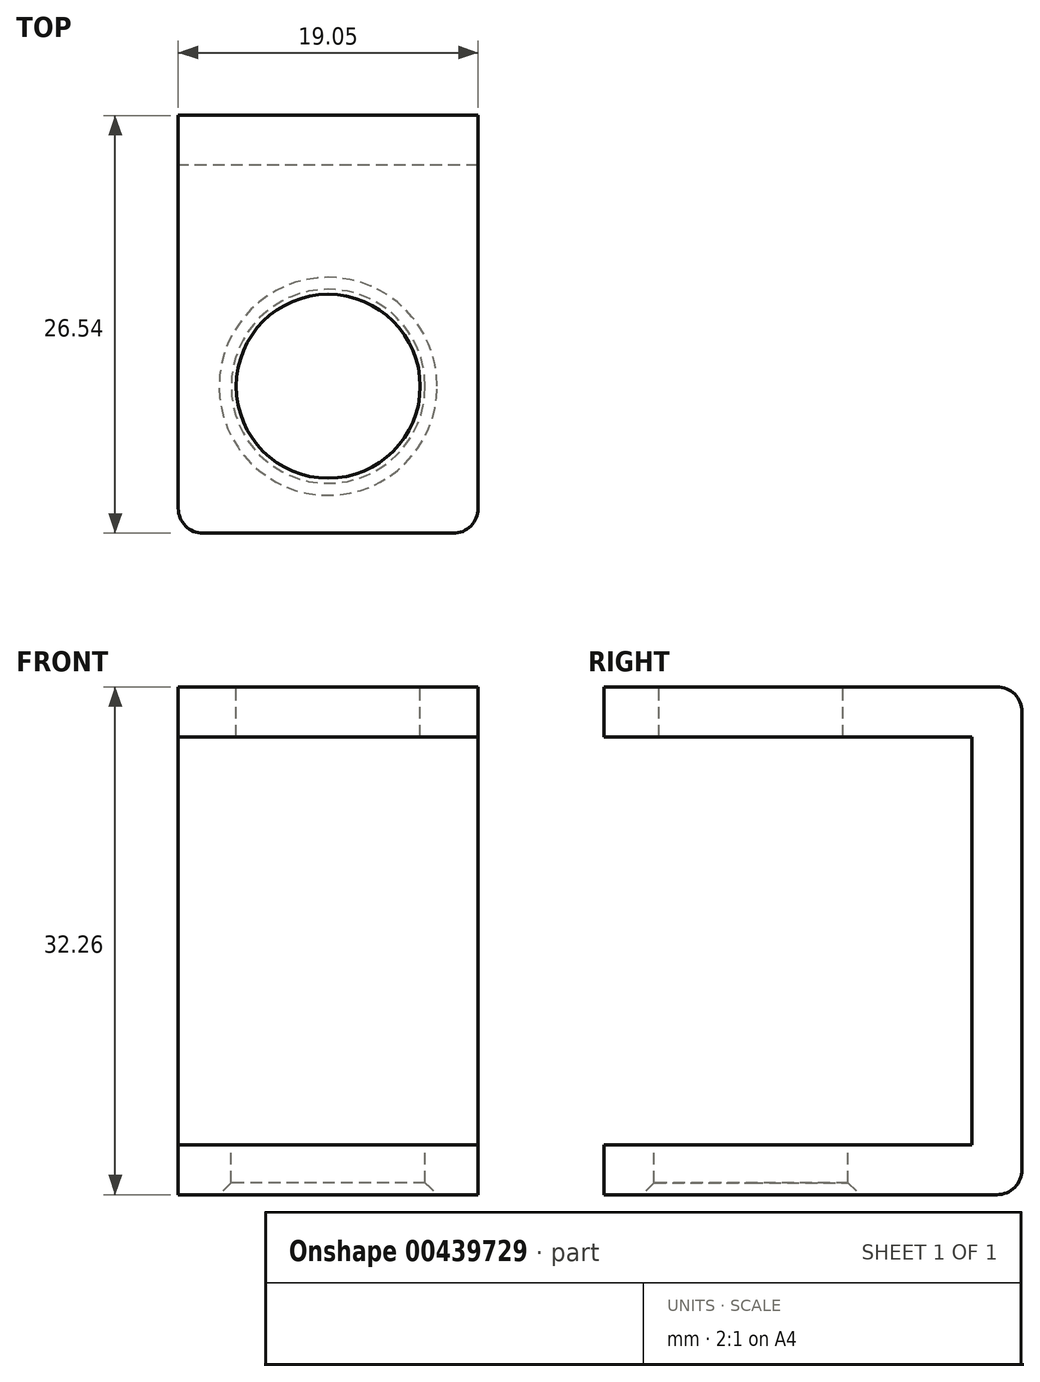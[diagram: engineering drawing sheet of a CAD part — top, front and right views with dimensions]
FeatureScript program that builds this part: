
annotation { "Feature Type Name" : "Feature", "Feature Type Description" : "" }
export const myFeature = defineFeature(function(context is Context, id is Id, definition is map)
    precondition{}
    {
        {
            var Q0;
            Q0=qCreatedBy(makeId("Right.planeOp"),FACE);
            var sketch = newSketch(context, id + "F0", { "sketchPlane" : qUnion([Q0])});
            skLineSegment(sketch, "E0.bottom", {"start": v(0, 0) * mm, "end": v(26.54, 0) * mm});
            skLineSegment(sketch, "E0.top", {"start": v(0, 3.18) * mm, "end": v(23.37, 3.18) * mm});
            skLineSegment(sketch, "E0.left", {"start": v(0, 0) * mm, "end": v(0, 3.18) * mm});
            skLineSegment(sketch, "E1.bottom", {"start": v(0, 32.26) * mm, "end": v(26.54, 32.26) * mm});
            skLineSegment(sketch, "E1.top", {"start": v(0, 29.08) * mm, "end": v(23.37, 29.08) * mm});
            skLineSegment(sketch, "E2", {"start": v(0, 32.26) * mm, "end": v(0, 29.08) * mm});
            skLineSegment(sketch, "E3", {"start": v(23.37, 3.18) * mm, "end": v(23.37, 29.08) * mm});
            skLineSegment(sketch, "E4", {"start": v(26.54, 0) * mm, "end": v(26.54, 32.26) * mm});
            skLineSegment(sketch, "E5", {"start": v(23.37, 29.08) * mm, "end": v(26.54, 29.08) * mm, "construction": true});
            skLineSegment(sketch, "E6", {"start": v(3.18, 21.78) * mm, "end": v(15.37, 21.78) * mm, "construction": true});
            skSolve(sketch);
        }
        {
            var Q0;
            Q0=qSketchRegion(id+"F0",true);
            extrude(context, id + "F1", {"entities" : qUnion([Q0]), "depth" : 19.05 * mm});
        }
        {
            var Q0;
            Q0=makeQuery(id+"F1.opExtrude","SWEPT_FACE",FACE,{"disambiguationData":[OSD([sQuery(id+"F0.wireOp",EDGE,"E0.top")])]});
            var sketch = newSketch(context, id + "F2", { "sketchPlane" : qUnion([Q0])});
            skCircle(sketch, "E7", {"center": v(9.53, 9.33) * mm, "radius": 6.16 * mm});
            skLineSegment(sketch, "E8", {"start": v(9.53, 0) * mm, "end": v(9.53, 9.33) * mm, "construction": true});
            skPoint(sketch, "E9.orphan", {"position": v(19.05, 11.68) * mm});
            skPoint(sketch, "E10", {"position": v(9.53, 3.18) * mm});
            skSolve(sketch);
        }
        {
            var Q0;
            Q0=qSketchRegion(id+"F2",true);
            extrude(context, id + "F3", {"entities" : qUnion([Q0]), "operationType" : NewBodyOperationType.REMOVE, "oppositeDirection" : true, "depth" : 25.4 * mm});
        }
        {
            var Q0;
            Q0=makeQuery(id+"F1.opExtrude","SWEPT_FACE",FACE,{"disambiguationData":[OSD([sQuery(id+"F0.wireOp",EDGE,"E1.bottom")])]});
            var sketch = newSketch(context, id + "F4", { "sketchPlane" : qUnion([Q0])});
            skCircle(sketch, "E11", {"center": v(9.53, 9.33) * mm, "radius": 5.84 * mm});
            skLineSegment(sketch, "E12", {"start": v(9.53, 9.33) * mm, "end": v(9.53, 0) * mm, "construction": true});
            skSolve(sketch);
        }
        {
            var Q0;
            Q0 = qSketchRegion(id + "F4", true);
            extrude(context, id + "F5", {"entities" : qUnion([Q0]), "operationType" : NewBodyOperationType.REMOVE, "endBound" : BoundingType.UP_TO_NEXT, "oppositeDirection" : true, "depth" : 25.4 * mm});
        }
        {
            var Q0;
            Q0=makeQuery(id+"F1.opExtrude","CAP_EDGE",EDGE,{"disambiguationData":[OSD([sQuery(id+"F0.wireOp",EDGE,"E2")])],"isStart":false});
            var Q1;
            Q1=makeQuery(id+"F1.opExtrude","CAP_EDGE",EDGE,{"disambiguationData":[OSD([sQuery(id+"F0.wireOp",EDGE,"E2")])],"isStart":true});
            var Q2;
            Q2=makeQuery(id+"F1.opExtrude","CAP_EDGE",EDGE,{"disambiguationData":[OSD([sQuery(id+"F0.wireOp",EDGE,"E0.left")])],"isStart":true});
            var Q3;
            Q3=makeQuery(id+"F1.opExtrude","CAP_EDGE",EDGE,{"disambiguationData":[OSD([sQuery(id+"F0.wireOp",EDGE,"E0.left")])],"isStart":false});
            var Q4;
            Q4=makeQuery(id+"F1.opExtrude","SWEPT_EDGE",EDGE,{"disambiguationData":[OSD([sQuery(id+"F0.wireOp",EDGE,"E1.bottom"),sQuery(id+"F0.wireOp",EDGE,"E4")])]});
            var Q5;
            Q5=makeQuery(id+"F1.opExtrude","SWEPT_EDGE",EDGE,{"disambiguationData":[OSD([sQuery(id+"F0.wireOp",EDGE,"E0.bottom"),sQuery(id+"F0.wireOp",EDGE,"E4")])]});
            fillet(context, id + "F6", {"entities" : qUnion([Q0, Q1, Q2, Q3, Q4, Q5]), "radius" : 1.59 * mm, "tangentPropagation" : true, "allowEdgeOverflow" : false});
        }
        {
            var Q0;
            Q0=makeQuery(id+"F3.boolean.opBoolean","INTERSECT",EDGE,{"derivedFrom":[makeQuery(id+"F1.opExtrude","SWEPT_FACE",FACE,{"disambiguationData":[OSD([sQuery(id+"F0.wireOp",EDGE,"E0.bottom")])]}),makeQuery(id+"F3.opExtrude","SWEPT_FACE",FACE,{"disambiguationData":[OSD([sQuery(id+"F2.wireOp",EDGE,"E7")])]})]});
            var Q1;
            Q1=makeQuery(id+"F5.boolean.opBoolean","COPY",EDGE,{"derivedFrom":makeQuery(id+"F5.opExtrude","CAP_EDGE",EDGE,{"disambiguationData":[OSD([sQuery(id+"F4.wireOp",EDGE,"E11")])],"isStart":false})});
            var Q2;
            Q2=makeQuery(id+"F5.boolean.opBoolean","COPY",EDGE,{"derivedFrom":makeQuery(id+"F5.opExtrude","CAP_EDGE",EDGE,{"disambiguationData":[OSD([sQuery(id+"F4.wireOp",EDGE,"E11")])],"isStart":true})});
            var Q3;
            Q3=makeQuery(id+"F3.boolean.opBoolean","COPY",EDGE,{"derivedFrom":makeQuery(id+"F3.opExtrude","CAP_EDGE",EDGE,{"disambiguationData":[OSD([sQuery(id+"F2.wireOp",EDGE,"E7")])],"isStart":true})});
            chamfer(context, id + "F7", {"entities" : qUnion([Q0, Q1, Q2, Q3]), "width" : 0.76 * mm, "tangentPropagation" : true});
        }
    });
